# Revit family: KW152 - Freespace
name_source: partatom
category: Communication Devices
revit_build: Autodesk Revit 2017 (Build: 20190508_0315(x64)
units: mm (PartAtom-declared; Revit-internal decimal feet)

## family parameters
Always vertical = No
Cut with Voids When Loaded = No
Maintain Annotation Orientation = No
Part Type = Normal
Room Calculation Point = No
Round Connector Dimension = Use Diameter
Shared = No
Work Plane-Based = Yes

## types (1)
- KW152 - Freespace
    Coverage Horizontal = 60.00°
    Coverage Vertical = 60.00°
    Default Elevation = 0 mm  [stored 0 ft]
    Depth = 386 mm
    Description = 15" 2-way Trapezoidal Loudspeaker
    Height = 816 mm
    Manufacturer = QSC Audio Products, LLC
    Manufacturer URL = www.qscaudio.com
    Model = KW152
    Product Documentation Link = https://www.qsc.com
    Product Page URL = https://www.qsc.com
    SPL Max = 133
    URL = https://www.qsc.com
    Voltage AC = 100-240VAC, 50-60Hz
    Weight Product (kg) = 29
    Weight Product (lb) = 64
    Width = 445 mm

note: [stored X ft] marks values corroborated as IEEE doubles in the binary element streams (Revit-internal decimal feet)

## geometry (parser evidence)
native form markers: Blend x4, Sweep x11
no freeform markers — native parametric forms only
